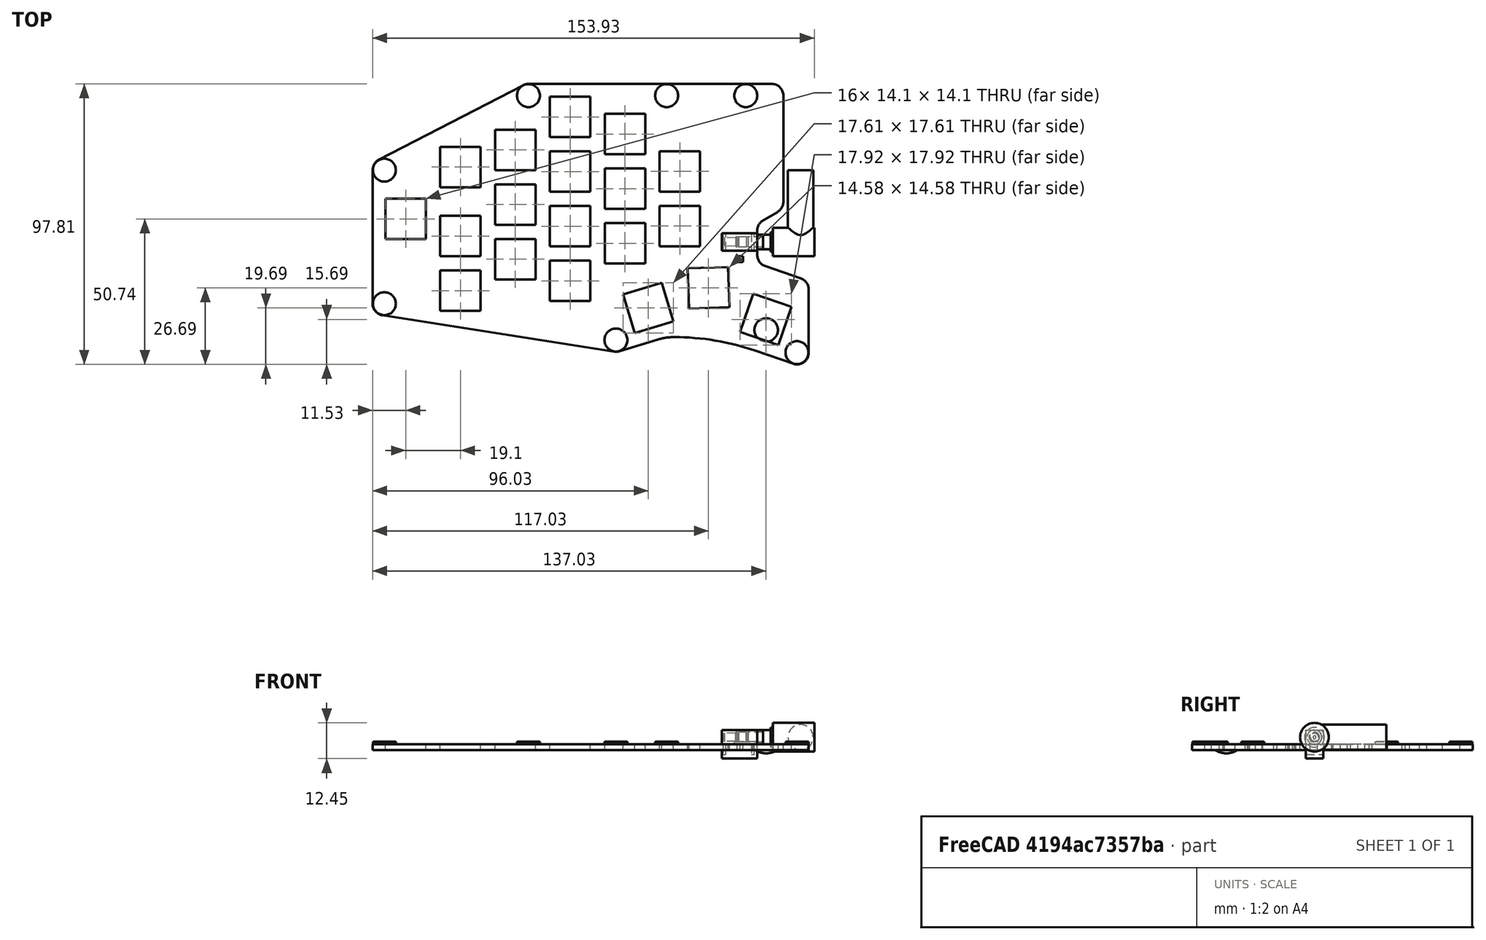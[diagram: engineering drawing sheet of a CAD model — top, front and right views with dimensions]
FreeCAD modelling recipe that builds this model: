
FCSTD DOCUMENT  (FreeCAD 0.21R33771 (Git))
Label: diy-keyboard
License: All rights reserved
LicenseURL: http://en.wikipedia.org/wiki/All_rights_reserved
objects: Sketcher::SketchObject×11, PartDesign::Pad×7, PartDesign::Body×5, PartDesign::ShapeBinder×3, PartDesign::Revolution×2, PartDesign::Pocket×2, Mesh::Feature×1, TechDraw::DrawSVGTemplate×1, PartDesign::SubShapeBinder×1, TechDraw::DrawViewPart×1, TechDraw::DrawPage×1
note: 42 computed .brp shape members not serialized (recipe doc carries the construction recipe); baked Part::Feature solids carry a one-line shape summary decoded from their .brp

FEATURE [Mesh::Feature] switch_mx
  Placement = pos=(43.4215,-43.9157,18) rot=(0,0,1;5.75959rad)
FEATURE [Sketcher::SketchObject] Sketch001  label="master-keys"
  FullyConstrained = false
  MapMode = 5
  Support = -> [XY_Plane]
  sketch-geometry (181):
    g0: GeomPoint X=-10 Y=-11 Z=0
    g1: LineSegment StartX=-16.7997 StartY=-18.2917 StartZ=0 EndX=-17.2917 EndY=-4.20034 EndZ=0
    g2: LineSegment StartX=-17.2917 StartY=-4.20034 StartZ=0 EndX=-3.20034 EndY=-3.70825 EndZ=0
    g3: LineSegment StartX=-3.20034 StartY=-3.70825 StartZ=0 EndX=-2.70825 EndY=-17.7997 EndZ=0
    g4: LineSegment StartX=-2.70825 StartY=-17.7997 StartZ=0 EndX=-16.7997 EndY=-18.2917 EndZ=0
    g5: LineSegment StartX=-19.1868 StartY=-20.8516 StartZ=0 EndX=-19.8516 EndY=-1.81322 EndZ=0
    g6: LineSegment StartX=-19.8516 StartY=-1.81322 StartZ=0 EndX=-0.81322 EndY=-1.14838 EndZ=0
    g7: LineSegment StartX=-0.81322 StartY=-1.14838 StartZ=0 EndX=-0.148385 EndY=-20.1868 EndZ=0
    g8: LineSegment StartX=-0.148385 StartY=-20.1868 StartZ=0 EndX=-19.1868 EndY=-20.8516 EndZ=0
    g9: GeomPoint X=-39.1 Y=4.5 Z=0
    g10: LineSegment StartX=-46.15 StartY=-2.55 StartZ=0 EndX=-46.15 EndY=11.55 EndZ=0
    g11: LineSegment StartX=-46.15 StartY=11.55 StartZ=0 EndX=-32.05 EndY=11.55 EndZ=0
    g12: LineSegment StartX=-32.05 StartY=11.55 StartZ=0 EndX=-32.05 EndY=-2.55 EndZ=0
    g13: LineSegment StartX=-32.05 StartY=-2.55 StartZ=0 EndX=-46.15 EndY=-2.55 EndZ=0
    g14: LineSegment StartX=-48.625 StartY=-5.025 StartZ=0 EndX=-48.625 EndY=14.025 EndZ=0
    g15: LineSegment StartX=-48.625 StartY=14.025 StartZ=0 EndX=-29.575 EndY=14.025 EndZ=0
    g16: LineSegment StartX=-29.575 StartY=14.025 StartZ=0 EndX=-29.575 EndY=-5.025 EndZ=0
    g17: LineSegment StartX=-29.575 StartY=-5.025 StartZ=0 EndX=-48.625 EndY=-5.025 EndZ=0
    g18: GeomPoint X=-58.2 Y=10.5 Z=0
    g19: LineSegment StartX=-65.25 StartY=3.45 StartZ=0 EndX=-65.25 EndY=17.55 EndZ=0
    g20: LineSegment StartX=-65.25 StartY=17.55 StartZ=0 EndX=-51.15 EndY=17.55 EndZ=0
    g21: LineSegment StartX=-51.15 StartY=17.55 StartZ=0 EndX=-51.15 EndY=3.45 EndZ=0
    g22: LineSegment StartX=-51.15 StartY=3.45 StartZ=0 EndX=-65.25 EndY=3.45 EndZ=0
    g23: LineSegment StartX=-67.725 StartY=0.975 StartZ=0 EndX=-67.725 EndY=20.025 EndZ=0
    g24: LineSegment StartX=-67.725 StartY=20.025 StartZ=0 EndX=-48.675 EndY=20.025 EndZ=0
    g25: LineSegment StartX=-48.675 StartY=20.025 StartZ=0 EndX=-48.675 EndY=0.975 EndZ=0
    g26: LineSegment StartX=-48.675 StartY=0.975 StartZ=0 EndX=-67.725 EndY=0.975 EndZ=0
    g27: GeomPoint X=-77.3 Y=-1 Z=0
    g28: LineSegment StartX=-84.35 StartY=-8.05 StartZ=0 EndX=-84.35 EndY=6.05 EndZ=0
    g29: LineSegment StartX=-84.35 StartY=6.05 StartZ=0 EndX=-70.25 EndY=6.05 EndZ=0
    g30: LineSegment StartX=-70.25 StartY=6.05 StartZ=0 EndX=-70.25 EndY=-8.05 EndZ=0
    g31: LineSegment StartX=-70.25 StartY=-8.05 StartZ=0 EndX=-84.35 EndY=-8.05 EndZ=0
    g32: LineSegment StartX=-86.825 StartY=-10.525 StartZ=0 EndX=-86.825 EndY=8.525 EndZ=0
    g33: LineSegment StartX=-86.825 StartY=8.525 StartZ=0 EndX=-67.775 EndY=8.525 EndZ=0
    g34: LineSegment StartX=-67.775 StartY=8.525 StartZ=0 EndX=-67.775 EndY=-10.525 EndZ=0
    g35: LineSegment StartX=-67.775 StartY=-10.525 StartZ=0 EndX=-86.825 EndY=-10.525 EndZ=0
    g36: GeomPoint X=-39.1 Y=23.55 Z=0
    g37: LineSegment StartX=-46.15 StartY=16.5 StartZ=0 EndX=-46.15 EndY=30.6 EndZ=0
    g38: LineSegment StartX=-46.15 StartY=30.6 StartZ=0 EndX=-32.05 EndY=30.6 EndZ=0
    g39: LineSegment StartX=-32.05 StartY=30.6 StartZ=0 EndX=-32.05 EndY=16.5 EndZ=0
    g40: LineSegment StartX=-32.05 StartY=16.5 StartZ=0 EndX=-46.15 EndY=16.5 EndZ=0
    g41: LineSegment StartX=-48.625 StartY=14.025 StartZ=0 EndX=-48.625 EndY=33.075 EndZ=0
    g42: LineSegment StartX=-48.625 StartY=33.075 StartZ=0 EndX=-29.575 EndY=33.075 EndZ=0
    g43: LineSegment StartX=-29.575 StartY=33.075 StartZ=0 EndX=-29.575 EndY=14.025 EndZ=0
    g44: LineSegment StartX=-29.575 StartY=14.025 StartZ=0 EndX=-48.625 EndY=14.025 EndZ=0
    g45: GeomPoint X=-20 Y=10.55 Z=0
    g46: LineSegment StartX=-27.05 StartY=3.5 StartZ=0 EndX=-27.05 EndY=17.6 EndZ=0
    g47: LineSegment StartX=-27.05 StartY=17.6 StartZ=0 EndX=-12.95 EndY=17.6 EndZ=0
    g48: LineSegment StartX=-12.95 StartY=17.6 StartZ=0 EndX=-12.95 EndY=3.5 EndZ=0
    g49: LineSegment StartX=-12.95 StartY=3.5 StartZ=0 EndX=-27.05 EndY=3.5 EndZ=0
    g50: LineSegment StartX=-29.525 StartY=1.025 StartZ=0 EndX=-29.525 EndY=20.075 EndZ=0
    g51: LineSegment StartX=-29.525 StartY=20.075 StartZ=0 EndX=-10.475 EndY=20.075 EndZ=0
    g52: LineSegment StartX=-10.475 StartY=20.075 StartZ=0 EndX=-10.475 EndY=1.025 EndZ=0
    g53: LineSegment StartX=-10.475 StartY=1.025 StartZ=0 EndX=-29.525 EndY=1.025 EndZ=0
    g54: GeomPoint X=-20 Y=29.6 Z=0
    g55: LineSegment StartX=-27.05 StartY=22.55 StartZ=0 EndX=-27.05 EndY=36.65 EndZ=0
    g56: LineSegment StartX=-27.05 StartY=36.65 StartZ=0 EndX=-12.95 EndY=36.65 EndZ=0
    g57: LineSegment StartX=-12.95 StartY=36.65 StartZ=0 EndX=-12.95 EndY=22.55 EndZ=0
    g58: LineSegment StartX=-12.95 StartY=22.55 StartZ=0 EndX=-27.05 EndY=22.55 EndZ=0
    g59: LineSegment StartX=-29.525 StartY=20.075 StartZ=0 EndX=-29.525 EndY=39.125 EndZ=0
    g60: LineSegment StartX=-29.525 StartY=39.125 StartZ=0 EndX=-10.475 EndY=39.125 EndZ=0
    g61: LineSegment StartX=-10.475 StartY=39.125 StartZ=0 EndX=-10.475 EndY=20.075 EndZ=0
    g62: LineSegment StartX=-10.475 StartY=20.075 StartZ=0 EndX=-29.525 EndY=20.075 EndZ=0
    g63: GeomPoint X=-39.1 Y=42.6 Z=0
    g64: LineSegment StartX=-46.15 StartY=35.55 StartZ=0 EndX=-46.15 EndY=49.65 EndZ=0
    g65: LineSegment StartX=-46.15 StartY=49.65 StartZ=0 EndX=-32.05 EndY=49.65 EndZ=0
    g66: LineSegment StartX=-32.05 StartY=49.65 StartZ=0 EndX=-32.05 EndY=35.55 EndZ=0
    g67: LineSegment StartX=-32.05 StartY=35.55 StartZ=0 EndX=-46.15 EndY=35.55 EndZ=0
    g68: LineSegment StartX=-48.625 StartY=33.075 StartZ=0 EndX=-48.625 EndY=52.125 EndZ=0
    g69: LineSegment StartX=-48.625 StartY=52.125 StartZ=0 EndX=-29.575 EndY=52.125 EndZ=0
    g70: LineSegment StartX=-29.575 StartY=52.125 StartZ=0 EndX=-29.575 EndY=33.075 EndZ=0
    g71: LineSegment StartX=-29.575 StartY=33.075 StartZ=0 EndX=-48.625 EndY=33.075 EndZ=0
    g72: GeomPoint X=-58.2 Y=29.55 Z=0
    g73: LineSegment StartX=-65.25 StartY=22.5 StartZ=0 EndX=-65.25 EndY=36.6 EndZ=0
    g74: LineSegment StartX=-65.25 StartY=36.6 StartZ=0 EndX=-51.15 EndY=36.6 EndZ=0
    g75: LineSegment StartX=-51.15 StartY=36.6 StartZ=0 EndX=-51.15 EndY=22.5 EndZ=0
    g76: LineSegment StartX=-51.15 StartY=22.5 StartZ=0 EndX=-65.25 EndY=22.5 EndZ=0
    g77: LineSegment StartX=-67.725 StartY=20.025 StartZ=0 EndX=-67.725 EndY=39.075 EndZ=0
    g78: LineSegment StartX=-67.725 StartY=39.075 StartZ=0 EndX=-48.675 EndY=39.075 EndZ=0
    g79: LineSegment StartX=-48.675 StartY=39.075 StartZ=0 EndX=-48.675 EndY=20.025 EndZ=0
    g80: LineSegment StartX=-48.675 StartY=20.025 StartZ=0 EndX=-67.725 EndY=20.025 EndZ=0
    g81: GeomPoint X=-77.3 Y=18.05 Z=0
    g82: LineSegment StartX=-84.35 StartY=11 StartZ=0 EndX=-84.35 EndY=25.1 EndZ=0
    g83: LineSegment StartX=-84.35 StartY=25.1 StartZ=0 EndX=-70.25 EndY=25.1 EndZ=0
    g84: LineSegment StartX=-70.25 StartY=25.1 StartZ=0 EndX=-70.25 EndY=11 EndZ=0
    g85: LineSegment StartX=-70.25 StartY=11 StartZ=0 EndX=-84.35 EndY=11 EndZ=0
    g86: LineSegment StartX=-86.825 StartY=8.525 StartZ=0 EndX=-86.825 EndY=27.575 EndZ=0
    g87: LineSegment StartX=-86.825 StartY=27.575 StartZ=0 EndX=-67.775 EndY=27.575 EndZ=0
    g88: LineSegment StartX=-67.775 StartY=27.575 StartZ=0 EndX=-67.775 EndY=8.525 EndZ=0
    g89: LineSegment StartX=-67.775 StartY=8.525 StartZ=0 EndX=-86.825 EndY=8.525 EndZ=0
    g90: GeomPoint X=-58.2 Y=48.6 Z=0
    g91: LineSegment StartX=-65.25 StartY=41.55 StartZ=0 EndX=-65.25 EndY=55.65 EndZ=0
    g92: LineSegment StartX=-65.25 StartY=55.65 StartZ=0 EndX=-51.15 EndY=55.65 EndZ=0
    g93: LineSegment StartX=-51.15 StartY=55.65 StartZ=0 EndX=-51.15 EndY=41.55 EndZ=0
    g94: LineSegment StartX=-51.15 StartY=41.55 StartZ=0 EndX=-65.25 EndY=41.55 EndZ=0
    g95: LineSegment StartX=-67.725 StartY=39.075 StartZ=0 EndX=-67.725 EndY=58.125 EndZ=0
    g96: LineSegment StartX=-67.725 StartY=58.125 StartZ=0 EndX=-48.675 EndY=58.125 EndZ=0
    g97: LineSegment StartX=-48.675 StartY=58.125 StartZ=0 EndX=-48.675 EndY=39.075 EndZ=0
    g98: LineSegment StartX=-48.675 StartY=39.075 StartZ=0 EndX=-67.725 EndY=39.075 EndZ=0
    g99: GeomPoint X=-77.3 Y=37.1 Z=0
    g100: LineSegment StartX=-84.35 StartY=30.05 StartZ=0 EndX=-84.35 EndY=44.15 EndZ=0
    g101: LineSegment StartX=-84.35 StartY=44.15 StartZ=0 EndX=-70.25 EndY=44.15 EndZ=0
    g102: LineSegment StartX=-70.25 StartY=44.15 StartZ=0 EndX=-70.25 EndY=30.05 EndZ=0
    g103: LineSegment StartX=-70.25 StartY=30.05 StartZ=0 EndX=-84.35 EndY=30.05 EndZ=0
    g104: LineSegment StartX=-86.825 StartY=27.575 StartZ=0 EndX=-86.825 EndY=46.625 EndZ=0
    g105: LineSegment StartX=-86.825 StartY=46.625 StartZ=0 EndX=-67.775 EndY=46.625 EndZ=0
    g106: LineSegment StartX=-67.775 StartY=46.625 StartZ=0 EndX=-67.775 EndY=27.575 EndZ=0
    g107: LineSegment StartX=-67.775 StartY=27.575 StartZ=0 EndX=-86.825 EndY=27.575 EndZ=0
    g108: GeomPoint X=-31 Y=-18 Z=0
    g109: LineSegment StartX=-35.6807 StartY=-26.8032 StartZ=0 EndX=-39.8032 EndY=-13.3193 EndZ=0
    g110: LineSegment StartX=-39.8032 StartY=-13.3193 StartZ=0 EndX=-26.3193 EndY=-9.19683 EndZ=0
    g111: LineSegment StartX=-26.3193 StartY=-9.19683 StartZ=0 EndX=-22.1968 EndY=-22.6807 EndZ=0
    g112: LineSegment StartX=-22.1968 StartY=-22.6807 StartZ=0 EndX=-35.6807 EndY=-26.8032 EndZ=0
    g113: LineSegment StartX=-37.324 StartY=-29.8936 StartZ=0 EndX=-42.8936 EndY=-11.676 EndZ=0
    g114: LineSegment StartX=-42.8936 StartY=-11.676 StartZ=0 EndX=-24.676 EndY=-6.10636 EndZ=0
    g115: LineSegment StartX=-24.676 StartY=-6.10636 StartZ=0 EndX=-19.1064 EndY=-24.324 EndZ=0
    g116: LineSegment StartX=-19.1064 StartY=-24.324 StartZ=0 EndX=-37.324 EndY=-29.8936 EndZ=0
    g117: GeomPoint X=10 Y=-22 Z=0
    g118: LineSegment StartX=1.03884 StartY=-26.3707 StartZ=0 EndX=5.62935 EndY=-13.0388 EndZ=0
    g119: LineSegment StartX=5.62935 StartY=-13.0388 StartZ=0 EndX=18.9612 EndY=-17.6293 EndZ=0
    g120: LineSegment StartX=18.9612 StartY=-17.6293 StartZ=0 EndX=14.3707 EndY=-30.9612 EndZ=0
    g121: LineSegment StartX=14.3707 StartY=-30.9612 StartZ=0 EndX=1.03884 EndY=-26.3707 EndZ=0
    g122: LineSegment StartX=-2.1071 StartY=-27.905 StartZ=0 EndX=4.09497 EndY=-9.8929 EndZ=0
    g123: LineSegment StartX=4.09497 StartY=-9.8929 StartZ=0 EndX=22.1071 EndY=-16.095 EndZ=0
    g124: LineSegment StartX=22.1071 StartY=-16.095 StartZ=0 EndX=15.905 EndY=-34.1071 EndZ=0
    g125: LineSegment StartX=15.905 StartY=-34.1071 StartZ=0 EndX=-2.1071 EndY=-27.905 EndZ=0
    g126: LineSegment StartX=-20 StartY=0 StartZ=0 EndX=-20 EndY=120 EndZ=0
    g127: LineSegment StartX=-39.1 StartY=0 StartZ=0 EndX=-39.1 EndY=120 EndZ=0
    g128: LineSegment StartX=-58.2 StartY=0 StartZ=0 EndX=-58.2 EndY=120 EndZ=0
    g129: LineSegment StartX=-77.3 StartY=0 StartZ=0 EndX=-77.3 EndY=120 EndZ=0
    g130: LineSegment StartX=-96.4 StartY=0 StartZ=0 EndX=-96.4 EndY=120 EndZ=0
    g131: GeomPoint X=-96.4 Y=-12 Z=0
    g132: LineSegment StartX=-103.45 StartY=-19.05 StartZ=0 EndX=-103.45 EndY=-4.95 EndZ=0
    g133: LineSegment StartX=-103.45 StartY=-4.95 StartZ=0 EndX=-89.35 EndY=-4.95 EndZ=0
    g134: LineSegment StartX=-89.35 StartY=-4.95 StartZ=0 EndX=-89.35 EndY=-19.05 EndZ=0
    g135: LineSegment StartX=-89.35 StartY=-19.05 StartZ=0 EndX=-103.45 EndY=-19.05 EndZ=0
    g136: LineSegment StartX=-105.925 StartY=-21.525 StartZ=0 EndX=-105.925 EndY=-2.475 EndZ=0
    g137: LineSegment StartX=-105.925 StartY=-2.475 StartZ=0 EndX=-86.875 EndY=-2.475 EndZ=0
    g138: LineSegment StartX=-86.875 StartY=-2.475 StartZ=0 EndX=-86.875 EndY=-21.525 EndZ=0
    g139: LineSegment StartX=-86.875 StartY=-21.525 StartZ=0 EndX=-105.925 EndY=-21.525 EndZ=0
    g140: GeomPoint X=-96.4 Y=7.05 Z=0
    g141: LineSegment StartX=-103.45 StartY=-5.4e-15 StartZ=0 EndX=-103.45 EndY=14.1 EndZ=0
    g142: LineSegment StartX=-103.45 StartY=14.1 StartZ=0 EndX=-89.35 EndY=14.1 EndZ=0
    g143: LineSegment StartX=-89.35 StartY=14.1 StartZ=0 EndX=-89.35 EndY=-1.8e-15 EndZ=0
    g144: LineSegment StartX=-89.35 StartY=-1.8e-15 StartZ=0 EndX=-103.45 EndY=-5.4e-15 EndZ=0
    g145: LineSegment StartX=-105.925 StartY=-2.475 StartZ=0 EndX=-105.925 EndY=16.575 EndZ=0
    g146: LineSegment StartX=-105.925 StartY=16.575 StartZ=0 EndX=-86.875 EndY=16.575 EndZ=0
    g147: LineSegment StartX=-86.875 StartY=16.575 StartZ=0 EndX=-86.875 EndY=-2.475 EndZ=0
    g148: LineSegment StartX=-86.875 StartY=-2.475 StartZ=0 EndX=-105.925 EndY=-2.475 EndZ=0
    g149: GeomPoint X=13.565 Y=0 Z=0
    g150: LineSegment StartX=-10 StartY=-11 StartZ=0 EndX=-10 EndY=9 EndZ=0
    g151: LineSegment StartX=-31 StartY=-18 StartZ=0 EndX=-31 EndY=2 EndZ=0
    g152: LineSegment StartX=10 StartY=-22 StartZ=0 EndX=10 EndY=-2 EndZ=0
    g153: LineSegment StartX=-1.50591 StartY=-29.2306 StartZ=0 EndX=-1.16158 EndY=-28.2306 EndZ=0
    g154: GeomPoint X=-96.4 Y=31.1 Z=0
    g155: LineSegment StartX=-103.45 StartY=24.05 StartZ=0 EndX=-103.45 EndY=38.15 EndZ=0
    g156: LineSegment StartX=-103.45 StartY=38.15 StartZ=0 EndX=-89.35 EndY=38.15 EndZ=0
    g157: LineSegment StartX=-89.35 StartY=38.15 StartZ=0 EndX=-89.35 EndY=24.05 EndZ=0
    g158: LineSegment StartX=-89.35 StartY=24.05 StartZ=0 EndX=-103.45 EndY=24.05 EndZ=0
    g159: LineSegment StartX=-105.925 StartY=21.575 StartZ=0 EndX=-105.925 EndY=40.625 EndZ=0
    g160: LineSegment StartX=-105.925 StartY=40.625 StartZ=0 EndX=-86.875 EndY=40.625 EndZ=0
    g161: LineSegment StartX=-86.875 StartY=40.625 StartZ=0 EndX=-86.875 EndY=21.575 EndZ=0
    g162: LineSegment StartX=-86.875 StartY=21.575 StartZ=0 EndX=-105.925 EndY=21.575 EndZ=0
    g163: GeomPoint X=-115.5 Y=13.05 Z=0
    g164: LineSegment StartX=-122.55 StartY=6 StartZ=0 EndX=-122.55 EndY=20.1 EndZ=0
    g165: LineSegment StartX=-122.55 StartY=20.1 StartZ=0 EndX=-108.45 EndY=20.1 EndZ=0
    g166: LineSegment StartX=-108.45 StartY=20.1 StartZ=0 EndX=-108.45 EndY=6 EndZ=0
    g167: LineSegment StartX=-108.45 StartY=6 StartZ=0 EndX=-122.55 EndY=6 EndZ=0
    g168: LineSegment StartX=-125.025 StartY=1.05 StartZ=0 EndX=-125.025 EndY=25.05 EndZ=0
    g169: LineSegment StartX=-125.025 StartY=25.05 StartZ=0 EndX=-105.975 EndY=25.05 EndZ=0
    g170: LineSegment StartX=-105.975 StartY=25.05 StartZ=0 EndX=-105.975 EndY=1.05 EndZ=0
    g171: LineSegment StartX=-105.975 StartY=1.05 StartZ=0 EndX=-125.025 EndY=1.05 EndZ=0
    g172: GeomPoint X=-58.2 Y=-8.55 Z=0
    g173: LineSegment StartX=-65.25 StartY=-15.6 StartZ=0 EndX=-65.25 EndY=-1.5 EndZ=0
    g174: LineSegment StartX=-65.25 StartY=-1.5 StartZ=0 EndX=-51.15 EndY=-1.5 EndZ=0
    g175: LineSegment StartX=-51.15 StartY=-1.5 StartZ=0 EndX=-51.15 EndY=-15.6 EndZ=0
    g176: LineSegment StartX=-51.15 StartY=-15.6 StartZ=0 EndX=-65.25 EndY=-15.6 EndZ=0
    g177: LineSegment StartX=-67.725 StartY=-18.075 StartZ=0 EndX=-67.725 EndY=0.975 EndZ=0
    g178: LineSegment StartX=-67.725 StartY=0.975 StartZ=0 EndX=-48.675 EndY=0.975 EndZ=0
    g179: LineSegment StartX=-48.675 StartY=0.975 StartZ=0 EndX=-48.675 EndY=-18.075 EndZ=0
    g180: LineSegment StartX=-48.675 StartY=-18.075 StartZ=0 EndX=-67.725 EndY=-18.075 EndZ=0
  constraints (453):
    c: Coincident(g1,g2)
    c: Coincident(g2,g3)
    c: Coincident(g3,g4)
    c: Coincident(g4,g1)
    c: Coincident(g5,g6)
    c: Coincident(g6,g7)
    c: Coincident(g7,g8)
    c: Coincident(g8,g5)
    c: Symmetric(g1,g3,g0)
    c: Symmetric(g5,g7,g0)
    c: Symmetric(g1,g2,g0)
    c: Symmetric(g5,g6,g0)
    c: Distance(g4) = 14.1
    c: Distance(g8) = 19.05
    c: Equal(g4,g1)
    c: Equal(g8,g5)
    c: Perpendicular(g1,g4)
    c: Parallel(g4,g8)
    c: Parallel(g1,g5)
    c: Coincident(g10,g11)
    c: Coincident(g11,g12)
    c: Coincident(g12,g13)
    c: Coincident(g13,g10)
    c: Coincident(g14,g15)
    c: Coincident(g15,g16)
    c: Coincident(g16,g17)
    c: Coincident(g17,g14)
    c: Symmetric(g10,g12,g9)
    c: Symmetric(g14,g16,g9)
    c: Symmetric(g10,g11,g9)
    c: Symmetric(g14,g15,g9)
    c: Equal(g4,g13) = 14
    c: Equal(g8,g17) = 19.05
    c: Equal(g13,g10)
    c: Equal(g17,g14)
    c: Perpendicular(g10,g13)
    c: Parallel(g13,g17)
    c: Parallel(g10,g14)
    c: Coincident(g19,g20)
    c: Coincident(g20,g21)
    c: Coincident(g21,g22)
    c: Coincident(g22,g19)
    c: Coincident(g23,g24)
    c: Coincident(g24,g25)
    c: Coincident(g25,g26)
    c: Coincident(g26,g23)
    c: Symmetric(g19,g21,g18)
    c: Symmetric(g23,g25,g18)
    c: Symmetric(g19,g20,g18)
    c: Symmetric(g23,g24,g18)
    c: Equal(g4,g22) = 14
    c: Equal(g8,g26) = 19.05
    c: Equal(g22,g19)
    c: Equal(g26,g23)
    c: Perpendicular(g19,g22)
    c: Parallel(g22,g26)
    c: Parallel(g19,g23)
    c: Coincident(g28,g29)
    c: Coincident(g29,g30)
    c: Coincident(g30,g31)
    c: Coincident(g31,g28)
    c: Coincident(g32,g33)
    c: Coincident(g33,g34)
    c: Coincident(g34,g35)
    c: Coincident(g35,g32)
    c: Symmetric(g28,g30,g27)
    c: Symmetric(g32,g34,g27)
    c: Symmetric(g28,g29,g27)
    c: Symmetric(g32,g33,g27)
    c: Equal(g4,g31) = 14
    c: Equal(g8,g35) = 19.05
    c: Equal(g31,g28)
    c: Equal(g35,g32)
    c: Perpendicular(g28,g31)
    c: Parallel(g31,g35)
    c: Parallel(g28,g32)
    c: Coincident(g37,g38)
    c: Coincident(g38,g39)
    c: Coincident(g39,g40)
    c: Coincident(g40,g37)
    c: Coincident(g41,g42)
    c: Coincident(g42,g43)
    c: Coincident(g43,g44)
    c: Coincident(g44,g41)
    c: Symmetric(g37,g39,g36)
    c: Symmetric(g41,g43,g36)
    c: Symmetric(g37,g38,g36)
    c: Symmetric(g41,g42,g36)
    c: Equal(g4,g40) = 14
    c: Equal(g8,g44) = 19.05
    c: Equal(g40,g37)
    c: Equal(g44,g41)
    c: Perpendicular(g37,g40)
    c: Parallel(g40,g44)
    c: Parallel(g37,g41)
    c: Coincident(g46,g47)
    c: Coincident(g47,g48)
    c: Coincident(g48,g49)
    c: Coincident(g49,g46)
    c: Coincident(g50,g51)
    c: Coincident(g51,g52)
    c: Coincident(g52,g53)
    c: Coincident(g53,g50)
    c: Symmetric(g46,g48,g45)
    c: Symmetric(g50,g52,g45)
    c: Symmetric(g46,g47,g45)
    c: Symmetric(g50,g51,g45)
    c: Equal(g4,g49) = 14
    c: Equal(g8,g53) = 19.05
    c: Equal(g49,g46)
    c: Equal(g53,g50)
    c: Perpendicular(g46,g49)
    c: Parallel(g49,g53)
    c: Parallel(g46,g50)
    c: Coincident(g55,g56)
    c: Coincident(g56,g57)
    c: Coincident(g57,g58)
    c: Coincident(g58,g55)
    c: Coincident(g59,g60)
    c: Coincident(g60,g61)
    c: Coincident(g61,g62)
    c: Coincident(g62,g59)
    c: Symmetric(g55,g57,g54)
    c: Symmetric(g59,g61,g54)
    c: Symmetric(g55,g56,g54)
    c: Symmetric(g59,g60,g54)
    c: Equal(g4,g58) = 14
    c: Equal(g8,g62) = 19.05
    c: Equal(g58,g55)
    c: Equal(g62,g59)
    c: Perpendicular(g55,g58)
    c: Parallel(g58,g62)
    c: Parallel(g55,g59)
    c: Coincident(g64,g65)
    c: Coincident(g65,g66)
    c: Coincident(g66,g67)
    c: Coincident(g67,g64)
    c: Coincident(g68,g69)
    c: Coincident(g69,g70)
    c: Coincident(g70,g71)
    c: Coincident(g71,g68)
    c: Symmetric(g64,g66,g63)
    c: Symmetric(g68,g70,g63)
    c: Symmetric(g64,g65,g63)
    c: Symmetric(g68,g69,g63)
    c: Equal(g4,g67) = 14
    c: Equal(g8,g71) = 19.05
    c: Equal(g67,g64)
    c: Equal(g71,g68)
    c: Perpendicular(g64,g67)
    c: Parallel(g67,g71)
    c: Parallel(g64,g68)
    c: Coincident(g73,g74)
    c: Coincident(g74,g75)
    c: Coincident(g75,g76)
    c: Coincident(g76,g73)
    c: Coincident(g77,g78)
    c: Coincident(g78,g79)
    c: Coincident(g79,g80)
    c: Coincident(g80,g77)
    c: Symmetric(g73,g75,g72)
    c: Symmetric(g77,g79,g72)
    c: Symmetric(g73,g74,g72)
    c: Symmetric(g77,g78,g72)
    c: Equal(g4,g76) = 14
    c: Equal(g8,g80) = 19.05
    c: Equal(g76,g73)
    c: Equal(g80,g77)
    c: Perpendicular(g73,g76)
    c: Parallel(g76,g80)
    c: Parallel(g73,g77)
    c: Coincident(g82,g83)
    c: Coincident(g83,g84)
    c: Coincident(g84,g85)
    c: Coincident(g85,g82)
    c: Coincident(g86,g87)
    c: Coincident(g87,g88)
    c: Coincident(g88,g89)
    c: Coincident(g89,g86)
    c: Symmetric(g82,g84,g81)
    c: Symmetric(g86,g88,g81)
    c: Symmetric(g82,g83,g81)
    c: Symmetric(g86,g87,g81)
    c: Equal(g4,g85) = 14
    c: Equal(g8,g89) = 19.05
    c: Equal(g85,g82)
    c: Equal(g89,g86)
    c: Perpendicular(g82,g85)
    c: Parallel(g85,g89)
    c: Parallel(g82,g86)
    c: Coincident(g91,g92)
    c: Coincident(g92,g93)
    c: Coincident(g93,g94)
    c: Coincident(g94,g91)
    c: Coincident(g95,g96)
    c: Coincident(g96,g97)
    c: Coincident(g97,g98)
    c: Coincident(g98,g95)
    c: Symmetric(g91,g93,g90)
    c: Symmetric(g95,g97,g90)
    c: Symmetric(g91,g92,g90)
    c: Symmetric(g95,g96,g90)
    c: Equal(g4,g94) = 14
    c: Equal(g8,g98) = 19.05
    c: Equal(g94,g91)
    c: Equal(g98,g95)
    c: Perpendicular(g91,g94)
    c: Parallel(g94,g98)
    c: Parallel(g91,g95)
    c: Coincident(g100,g101)
    c: Coincident(g101,g102)
    c: Coincident(g102,g103)
    c: Coincident(g103,g100)
    c: Coincident(g104,g105)
    c: Coincident(g105,g106)
    c: Coincident(g106,g107)
    c: Coincident(g107,g104)
    c: Symmetric(g100,g102,g99)
    c: Symmetric(g104,g106,g99)
    c: Symmetric(g100,g101,g99)
    c: Symmetric(g104,g105,g99)
    c: Equal(g4,g103) = 14
    c: Equal(g8,g107) = 19.05
    c: Equal(g103,g100)
    c: Equal(g107,g104)
    c: Perpendicular(g100,g103)
    c: Parallel(g103,g107)
    c: Parallel(g100,g104)
    c: Coincident(g109,g110)
    c: Coincident(g110,g111)
    c: Coincident(g111,g112)
    c: Coincident(g112,g109)
    c: Coincident(g113,g114)
    c: Coincident(g114,g115)
    c: Coincident(g115,g116)
    c: Coincident(g116,g113)
    c: Symmetric(g109,g111,g108)
    c: Symmetric(g113,g115,g108)
    c: Symmetric(g109,g110,g108)
    c: Symmetric(g113,g114,g108)
    c: Equal(g4,g112) = 14
    c: Equal(g8,g116) = 19.05
    c: Equal(g112,g109)
    c: Equal(g116,g113)
    c: Perpendicular(g109,g112)
    c: Parallel(g112,g116)
    c: Parallel(g109,g113)
    c: Coincident(g118,g119)
    c: Coincident(g119,g120)
    c: Coincident(g120,g121)
    c: Coincident(g121,g118)
    c: Coincident(g122,g123)
    c: Coincident(g123,g124)
    c: Coincident(g124,g125)
    c: Coincident(g125,g122)
    c: Symmetric(g118,g120,g117)
    c: Symmetric(g122,g124,g117)
    c: Symmetric(g118,g119,g117)
    c: Symmetric(g122,g123,g117)
    c: Equal(g4,g121) = 14
    c: Equal(g8,g125) = 19.05
    c: Equal(g121,g118)
    c: Equal(g125,g122)
    c: Perpendicular(g118,g121)
    c: Parallel(g121,g125)
    c: Parallel(g118,g122)
    c: PointOnObject(g126,g-1)
    c: DistanceY(g126,g126) = 120
    c: PointOnObject(g45,g126)
    c: PointOnObject(g54,g126)
    c: Distance(g45,g54) = 19.05
    c: PointOnObject(g127,g-1)
    c: Horizontal(g127,g126)
    c: PointOnObject(g128,g-1)
    c: PointOnObject(g129,g-1)
    c: Horizontal(g129,g128)
    c: Horizontal(g128,g127)
    c: PointOnObject(g9,g127)
    c: PointOnObject(g36,g127)
    c: PointOnObject(g63,g127)
    c: PointOnObject(g18,g128)
    c: PointOnObject(g72,g128)
    c: PointOnObject(g90,g128)
    c: PointOnObject(g27,g129)
    c: PointOnObject(g81,g129)
    c: PointOnObject(g99,g129)
    c: Parallel(g70,g127)
    c: Parallel(g43,g127)
    c: Parallel(g127,g16)
    c: Distance(g9,g36) = 19.05
    c: Distance(g36,g63) = 19.05
    c: Parallel(g25,g128)
    c: Parallel(g79,g128)
    c: Parallel(g97,g128)
    c: Parallel(g106,g129)
    c: Parallel(g88,g129)
    c: Parallel(g34,g129)
    c: Distance(g18,g72) = 19.05
    c: Distance(g72,g90) = 19.05
    c: Distance(g27,g81) = 19.05
    c: Distance(g81,g99) = 19.05
    c: Angle(g-1,g128) = 1.5708
    c: Angle(g-1,g129) = 1.5708
    c: PointOnObject(g130,g-1)
    c: Horizontal(g130,g129)
    c: Angle(g-1,g130) = 1.5708
    c: Coincident(g132,g133)
    c: Coincident(g133,g134)
    c: Coincident(g134,g135)
    c: Coincident(g135,g132)
    c: Coincident(g136,g137)
    c: Coincident(g137,g138)
    c: Coincident(g138,g139)
    c: Coincident(g139,g136)
    c: Symmetric(g132,g134,g131)
    c: Symmetric(g136,g138,g131)
    c: Symmetric(g132,g133,g131)
    c: Symmetric(g136,g137,g131)
    c: Equal(g4,g135) = 14
    c: Equal(g8,g139) = 19.05
    c: Equal(g135,g132)
    c: Equal(g139,g136)
    c: Perpendicular(g132,g135)
    c: Parallel(g135,g139)
    c: Parallel(g132,g136)
    c: Coincident(g141,g142)
    c: Coincident(g142,g143)
    c: Coincident(g143,g144)
    c: Coincident(g144,g141)
    c: Coincident(g145,g146)
    c: Coincident(g146,g147)
    c: Coincident(g147,g148)
    c: Coincident(g148,g145)
    c: Symmetric(g141,g143,g140)
    c: Symmetric(g145,g147,g140)
    c: Symmetric(g141,g142,g140)
    c: Symmetric(g145,g146,g140)
    c: Equal(g4,g144) = 14
    c: Equal(g8,g148) = 19.05
    c: Equal(g144,g141)
    c: Equal(g148,g145)
    c: Perpendicular(g141,g144)
    c: Parallel(g144,g148)
    c: Parallel(g141,g145)
    c: PointOnObject(g140,g130)
    c: PointOnObject(g131,g130)
    c: Parallel(g138,g130)
    c: Parallel(g130,g147)
    c: Distance(g140,g131) = 19.05
    c: Perpendicular(g-1,g127)
    c: Parallel(g61,g126)
    c: Parallel(g52,g126)
    c: Parallel(g126,g127)
    c: DistanceX(g127,g126) = 19.1
    c: DistanceY(g127,g9) = 4.5
    c: DistanceX(g128,g127) = 19.1
    c: DistanceY(g128,g18) = 10.5
    c: DistanceX(g129,g128) = 19.1
    c: DistanceY(g129,g27) = -1
    c: DistanceX(g130,g129) = 19.1
    c: PointOnObject(g149,g-1)
    c: DistanceX(g126,g-1) = 20
    c: DistanceX(g0,g-1) = 10
    c: DistanceY(g117,g-1) = 22
    c: DistanceY(g108,g-1) = 18
    c: Coincident(g150,g0)
    c: Vertical(g150)
    c: Coincident(g151,g108)
    c: Coincident(g152,g117)
    c: Vertical(g152)
    c: Vertical(g151)
    c: Equal(g151,g150)
    c: Equal(g150,g152)
    c: DistanceY(g152,g152) = 20
    c: Angle(g151,g111) = 0.296706
    c: DistanceY(g45,g36) = 13
    c: Angle(g120,g152) = 0.331613
    c: PointOnObject(g153,g125)
    c: Perpendicular(g125,g153)
    c: DistanceY(g153,g153) = 1
    c: Distance(g153,g122) = 1
    c: DistanceY(g131,g130) = 12
    c: Coincident(g155,g156)
    c: Coincident(g156,g157)
    c: Coincident(g157,g158)
    c: Coincident(g158,g155)
    c: Coincident(g159,g160)
    c: Coincident(g160,g161)
    c: Coincident(g161,g162)
    c: Coincident(g162,g159)
    c: Symmetric(g155,g157,g154)
    c: Symmetric(g159,g161,g154)
    c: Symmetric(g155,g156,g154)
    c: Symmetric(g159,g160,g154)
    c: Equal(g158,g155)
    c: Equal(g162,g159)
    c: Perpendicular(g155,g158)
    c: Parallel(g158,g162)
    c: Parallel(g155,g159)
    c: PointOnObject(g154,g130)
    c: Parallel(g157,g130)
    c: Equal(g162,g146)
    c: Equal(g158,g142)
    c: Angle(g150,g3) = 0.0349066
    c: DistanceY(g0,g-1) = 11
    c: DistanceX(g0,g117) = 20
    c: DistanceX(g108,g0) = 21
    c: Coincident(g164,g165)
    c: Coincident(g165,g166)
    c: Coincident(g166,g167)
    c: Coincident(g167,g164)
    c: Coincident(g168,g169)
    c: Coincident(g169,g170)
    c: Coincident(g170,g171)
    c: Coincident(g171,g168)
    c: Symmetric(g164,g166,g163)
    c: Symmetric(g168,g170,g163)
    c: Symmetric(g164,g165,g163)
    c: Symmetric(g168,g169,g163)
    c: Perpendicular(g164,g167)
    c: Parallel(g167,g171)
    c: Parallel(g164,g168)
    c: Equal(g169,g137)
    c: Equal(g165,g133)
    c: Horizontal(g169)
    c: DistanceX(g163,g130) = 19.1
    c: DistanceY(g163,g140) = -6
    c: DistanceY(g168,g168) = 24
    c: Equal(g164,g165)
    c: Coincident(g173,g174)
    c: Coincident(g174,g175)
    c: Coincident(g175,g176)
    c: Coincident(g176,g173)
    c: Coincident(g177,g178)
    c: Coincident(g178,g179)
    c: Coincident(g179,g180)
    c: Coincident(g180,g177)
    c: Symmetric(g173,g175,g172)
    c: Symmetric(g177,g179,g172)
    c: Symmetric(g173,g174,g172)
    c: Symmetric(g177,g178,g172)
    c: Equal(g176,g173)
    c: Equal(g180,g177)
    c: Perpendicular(g173,g176)
    c: Parallel(g176,g180)
    c: Parallel(g173,g177)
    c: Equal(g178,g26)
    c: Equal(g174,g22)
    c: Horizontal(g178)
    c: DistanceY(g172,g18) = 19.05
    c: Vertical(g172,g18)
    c: DistanceY(g154,g99) = 6
    c: DistanceY(g145,g159) = 5
FEATURE [Sketcher::SketchObject] Sketch
  FullyConstrained = false
  MapMode = 5
  Placement = pos=(0,0,0) rot=(1,0,0;1.5708rad)
  Support = -> [XZ_Plane001]
  sketch-geometry (7):
    g0: LineSegment StartX=0 StartY=-1.3 StartZ=0 EndX=0 EndY=0 EndZ=0
    g1: LineSegment StartX=0 StartY=0 StartZ=0 EndX=4.1 EndY=0 EndZ=0
    g2: ArcOfEllipse CenterX=0 CenterY=5.61097 CenterZ=0 NormalX=0 NormalY=0 NormalZ=1 MajorRadius=7.02288 MinorRadius=6.91097 AngleXU=3.14159 StartAngle=1.5708 EndAngle=2.19421
    g3: LineSegment StartX=-7.02288 StartY=5.61097 StartZ=0 EndX=7.02288 EndY=5.61097 EndZ=0
    g4: LineSegment StartX=0 StartY=-1.3 StartZ=0 EndX=0 EndY=12.5219 EndZ=0
    g5: GeomPoint X=-1.24876 Y=5.61097 Z=0
    g6: GeomPoint X=1.24876 Y=5.61097 Z=0
  constraints (11):
    c: Horizontal(g1)
    c: Vertical(g0)
    c: InternalAlignment(g3-g6 -> g2) x4
    c: Coincident(g2,g0)
    c: Coincident(g1,g0)
    c: Coincident(g1,g2)
    c: DistanceX(g1,g1) = 4.1
    c: Coincident(g4,g0)
    c: Vertical(g4)
    c: DistanceY(g0,g0) = 1.3
    c: Coincident(g0,g-1)
FEATURE [PartDesign::Revolution] Revolution
  Angle = 360
  Axis = (0,2e-16,1)
  Base = (0,0,0)
  Placement = pos=(0,0,0) rot=(1,0,0;1.5708rad)
  Profile = -> Sketch
  ReferenceAxis = -> Sketch [V_Axis]
  Reversed = true
FEATURE [PartDesign::Body] Body001  label="rubber-foot"
  Group = -> [Sketch,Revolution]
  Origin = -> Origin001
  Placement = pos=(10.1,-25.7,0.2) rot=(0,0,1;0rad)
  Tip = -> Revolution
FEATURE [Sketcher::SketchObject] Sketch004  label="master-mcu"
  ExternalGeometry = -> [Sketch001]
  FullyConstrained = false
  MapMode = 5
  Support = -> [XY_Plane]
  sketch-geometry (7):
    g0: LineSegment StartX=-6.5 StartY=25.125 StartZ=0 EndX=12.5 EndY=25.125 EndZ=0
    g1: LineSegment StartX=12.5 StartY=25.125 StartZ=0 EndX=12.5 EndY=59.125 EndZ=0
    g2: LineSegment StartX=12.5 StartY=59.125 StartZ=0 EndX=-6.5 EndY=59.125 EndZ=0
    g3: LineSegment StartX=-6.5 StartY=59.125 StartZ=0 EndX=-6.5 EndY=25.125 EndZ=0
    g4: GeomPoint X=-2.62 Y=29.125 Z=0
    g5: GeomPoint X=12.62 Y=29.125 Z=0
    g6: GeomPoint X=3 Y=42.125 Z=0
  constraints (12):
    c: Coincident(g0,g1)
    c: Coincident(g1,g2)
    c: Coincident(g2,g3)
    c: Coincident(g3,g0)
    c: Symmetric(g0,g1,g6)
    c: Symmetric(g0,g2,g6)
    c: Distance(g2) = 19
    c: Distance(g3) = 34
    c: Perpendicular(g3,g2)
    c: DistanceX(g-1,g6) = 3
    c: Horizontal(g2)
    c: DistanceY(g2,g-3) = -7
FEATURE [Sketcher::SketchObject] Sketch005
  FullyConstrained = true
  MapMode = 5
  Placement = pos=(0,0,0) rot=(1,0,0;1.5708rad)
  Support = -> [XZ_Plane002]
  sketch-geometry (4):
    g0: LineSegment StartX=-3.05 StartY=2.55 StartZ=0 EndX=3.05 EndY=2.55 EndZ=0
    g1: LineSegment StartX=3.05 StartY=2.55 StartZ=0 EndX=3.05 EndY=-2.55 EndZ=0
    g2: LineSegment StartX=3.05 StartY=-2.55 StartZ=0 EndX=-3.05 EndY=-2.55 EndZ=0
    g3: LineSegment StartX=-3.05 StartY=-2.55 StartZ=0 EndX=-3.05 EndY=2.55 EndZ=0
  constraints (11):
    c: Coincident(g0,g1)
    c: Coincident(g1,g2)
    c: Coincident(g2,g3)
    c: Coincident(g3,g0)
    c: Horizontal(g0)
    c: Horizontal(g2)
    c: Vertical(g1)
    c: Vertical(g3)
    c: Symmetric(g0,g1,g-1)
    c: DistanceX(g0,g0) = 6.1
    c: DistanceY(g1,g1) = 5.1
FEATURE [PartDesign::Pad] Pad005
  Direction = (0,-1,-2e-16)
  Length = 12.3
  Length2 = 10
  Placement = pos=(0,0,0) rot=(1,0,0;1.5708rad)
  Profile = -> Sketch005
  ReferenceAxis = -> Sketch005 [N_Axis]
  Reversed = true
  Type = 0
FEATURE [Sketcher::SketchObject] Sketch006
  FullyConstrained = false
  MapMode = 5
  Placement = pos=(0,0,0) rot=(1,0,0;1.5708rad)
  Support = -> [XZ_Plane002]
  sketch-geometry (2):
    g0: Circle CenterX=0 CenterY=0 CenterZ=0 NormalX=0 NormalY=0 NormalZ=1 AngleXU=0 Radius=2.55
    g1: Circle CenterX=-0.041022 CenterY=0 CenterZ=0 NormalX=0 NormalY=0 NormalZ=1 AngleXU=0 Radius=1.8
  constraints (4):
    c: Coincident(g0,g-1)
    c: Diameter(g0) = 5.1
    c: PointOnObject(g1,g-1)
    c: Diameter(g1) = 3.6
FEATURE [PartDesign::Pad] Pad006
  BaseFeature = -> Pad005
  Direction = (0,-1,-2e-16)
  Length = 2
  Length2 = 10
  Placement = pos=(0,0,0) rot=(1,0,0;1.5708rad)
  Profile = -> Sketch006
  ReferenceAxis = -> Sketch006 [N_Axis]
  Type = 0
FEATURE [Sketcher::SketchObject] Sketch007
  FullyConstrained = true
  MapMode = 5
  Placement = pos=(0,0,0) rot=(0.57735,0.57735,0.57735;2.0944rad)
  Support = -> [YZ_Plane002]
  sketch-geometry (8):
    g0: LineSegment StartX=1 StartY=0 StartZ=0 EndX=2 EndY=0 EndZ=0
    g1: LineSegment StartX=2 StartY=0 StartZ=0 EndX=2 EndY=-6 EndZ=0
    g2: LineSegment StartX=2 StartY=-6 StartZ=0 EndX=1 EndY=-6 EndZ=0
    g3: LineSegment StartX=1 StartY=-6 StartZ=0 EndX=1 EndY=0 EndZ=0
    g4: LineSegment StartX=11 StartY=0 StartZ=0 EndX=12 EndY=0 EndZ=0
    g5: LineSegment StartX=12 StartY=0 StartZ=0 EndX=12 EndY=-6 EndZ=0
    g6: LineSegment StartX=12 StartY=-6 StartZ=0 EndX=11 EndY=-6 EndZ=0
    g7: LineSegment StartX=11 StartY=-6 StartZ=0 EndX=11 EndY=0 EndZ=0
  constraints (24):
    c: Coincident(g0,g1)
    c: Coincident(g1,g2)
    c: Coincident(g2,g3)
    c: Coincident(g3,g0)
    c: Horizontal(g0)
    c: Horizontal(g2)
    c: Vertical(g1)
    c: Vertical(g3)
    c: Coincident(g4,g5)
    c: Coincident(g5,g6)
    c: Coincident(g6,g7)
    c: Coincident(g7,g4)
    c: Horizontal(g4)
    c: Horizontal(g6)
    c: Vertical(g5)
    c: Vertical(g7)
    c: PointOnObject(g4,g-1)
    c: PointOnObject(g0,g-1)
    c: DistanceX(g2,g2) = 1
    c: Equal(g2,g6)
    c: DistanceY(g3,g3) = 6
    c: Horizontal(g2,g6)
    c: DistanceX(g-1,g0) = 1
    c: DistanceX(g-1,g4) = 11
FEATURE [PartDesign::Pad] Pad007
  BaseFeature = -> Pad006
  Direction = (1,-2e-16,3e-16)
  Length = 6
  Length2 = 10
  Midplane = true
  Placement = pos=(0,0,0) rot=(1,0,0;1.5708rad)
  Profile = -> Sketch007
  ReferenceAxis = -> Sketch007 [N_Axis]
  Type = 0
FEATURE [PartDesign::Body] Body002  label="trrs-connector"
  Group = -> [Sketch005,Pad005,Sketch006,Pad006,Sketch007,Pad007]
  Origin = -> Origin002
  Placement = pos=(7,5,4.5) rot=(0,0,1;1.5708rad)
  Tip = -> Pad007
FEATURE [Sketcher::SketchObject] Sketch015  label="master-pcb-shape"
  ExternalGeometry = -> [Sketch001,Sketch004]
  FullyConstrained = true
  MapMode = 5
  Support = -> [XY_Plane]
  sketch-geometry (35):
    g0: Circle CenterX=-72.725 CenterY=56.025 CenterZ=0 NormalX=0 NormalY=0 NormalZ=1 AngleXU=0 Radius=4
    g1: Circle CenterX=-24.575 CenterY=56.025 CenterZ=0 NormalX=0 NormalY=0 NormalZ=1 AngleXU=0 Radius=4
    g2: Circle CenterX=20.8436 CenterY=-33.5866 CenterZ=0 NormalX=0 NormalY=0 NormalZ=1 AngleXU=0 Radius=4
    g3: Circle CenterX=-42.2413 CenterY=-29.2011 CenterZ=0 NormalX=0 NormalY=0 NormalZ=1 AngleXU=0 Radius=4
    g4: Circle CenterX=-122.925 CenterY=30.05 CenterZ=0 NormalX=0 NormalY=0 NormalZ=1 AngleXU=0 Radius=4
    g5: Circle CenterX=-122.925 CenterY=-16.525 CenterZ=0 NormalX=0 NormalY=0 NormalZ=1 AngleXU=0 Radius=4
    g6: ArcOfCircle CenterX=-72.725 CenterY=56.025 CenterZ=0 NormalX=0 NormalY=0 NormalZ=1 AngleXU=0 Radius=4.1 StartAngle=1.5708 EndAngle=2.04829
    g7: ArcOfCircle CenterX=-122.925 CenterY=30.05 CenterZ=0 NormalX=0 NormalY=0 NormalZ=1 AngleXU=0 Radius=4.1 StartAngle=2.04829 EndAngle=3.14159
    g8: LineSegment StartX=-127.025 StartY=30.05 StartZ=0 EndX=-127.025 EndY=-16.525 EndZ=0
    g9: ArcOfCircle CenterX=-122.925 CenterY=-16.525 CenterZ=0 NormalX=0 NormalY=0 NormalZ=1 AngleXU=0 Radius=4.1 StartAngle=3.14159 EndAngle=4.55655
    g10: ArcOfCircle CenterX=20.8436 CenterY=-33.5866 CenterZ=0 NormalX=0 NormalY=0 NormalZ=1 AngleXU=0 Radius=4.1 StartAngle=4.38078 EndAngle=6.28319
    g11: Circle CenterX=3 CenterY=56.025 CenterZ=0 NormalX=0 NormalY=0 NormalZ=1 AngleXU=0 Radius=4
    g12: LineSegment StartX=-124.809 StartY=33.6914 StartZ=0 EndX=-74.6092 EndY=59.6664 EndZ=0
    g13: ArcOfCircle CenterX=12 CenterY=56.025 CenterZ=0 NormalX=0 NormalY=0 NormalZ=1 AngleXU=0 Radius=4.1 StartAngle=0 EndAngle=1.5708
    g14: LineSegment StartX=24.9436 StartY=-33.5866 StartZ=0 EndX=24.9436 EndY=-11.5866 EndZ=0
    g15: ArcOfCircle CenterX=20.8436 CenterY=-11.5866 CenterZ=0 NormalX=0 NormalY=0 NormalZ=1 AngleXU=0 Radius=4.1 StartAngle=0 EndAngle=1.23918
    g16: ArcOfCircle CenterX=-42.2413 CenterY=-29.2011 CenterZ=0 NormalX=0 NormalY=0 NormalZ=1 AngleXU=0 Radius=4.1 StartAngle=4.55655 EndAngle=5.00909
    g17: LineSegment StartX=-72.725 StartY=60.125 StartZ=0 EndX=12 EndY=60.125 EndZ=0
    g18: LineSegment StartX=-28.2152 StartY=-27.1088 StartZ=0 EndX=-27.6304 EndY=-29.0214 EndZ=0
    g19: LineSegment StartX=6.89896 StartY=-31.0061 StartZ=0 EndX=6.24783 EndY=-32.8971 EndZ=0
    g20: LineSegment StartX=6.24783 StartY=-32.8971 StartZ=0 EndX=19.5087 EndY=-37.4632 EndZ=0
    g21: LineSegment StartX=-41.0426 StartY=-33.1219 StartZ=0 EndX=-27.6304 EndY=-29.0214 EndZ=0
    g22: ArcOfCircle CenterX=-21.9687 CenterY=-47.5399 CenterZ=0 NormalX=0 NormalY=0 NormalZ=1 AngleXU=0 Radius=19.3647 StartAngle=1.5708 EndAngle=1.8675
    g23: ArcOfCircle CenterX=-21.9687 CenterY=-114.844 CenterZ=0 NormalX=0 NormalY=0 NormalZ=1 AngleXU=0 Radius=86.6687 StartAngle=1.23918 EndAngle=1.5708
    g24: LineSegment StartX=3 StartY=56.025 StartZ=0 EndX=3 EndY=59.125 EndZ=0
    g25: LineSegment StartX=16.1 StartY=56.025 StartZ=0 EndX=16.1 EndY=19 EndZ=0
    g26: LineSegment StartX=7 StartY=0.440896 StartZ=0 EndX=7 EndY=9 EndZ=0
    g27: ArcOfCircle CenterX=11.1 CenterY=9 CenterZ=0 NormalX=0 NormalY=0 NormalZ=1 AngleXU=0 Radius=4.1 StartAngle=2.09617 EndAngle=3.14159
    g28: ArcOfCircle CenterX=12 CenterY=19 CenterZ=0 NormalX=0 NormalY=0 NormalZ=1 AngleXU=0 Radius=4.1 StartAngle=5.23776 EndAngle=6.28319
    g29: ArcOfCircle CenterX=11.1 CenterY=0.440896 CenterZ=0 NormalX=0 NormalY=0 NormalZ=1 AngleXU=0 Radius=4.1 StartAngle=3.14159 EndAngle=4.38078
    g30: LineSegment StartX=9.04371 StartY=12.5471 StartZ=0 EndX=14.0563 EndY=15.4529 EndZ=0
    g31: LineSegment StartX=9.76517 StartY=-3.43573 StartZ=0 EndX=22.1784 EndY=-7.70994 EndZ=0
    g32: LineSegment StartX=16.5887 StartY=-32.1215 StartZ=0 EndX=20.8436 EndY=-33.5866 EndZ=0
    g33: LineSegment StartX=-42.2413 StartY=-29.2011 StartZ=0 EndX=-37.9379 EndY=-27.8854 EndZ=0
    g34: LineSegment StartX=-42.8777 StartY=-33.2514 StartZ=0 EndX=-123.561 EndY=-20.5753 EndZ=0
  constraints (95):
    c: Equal(g3,g4)
    c: Equal(g4,g0)
    c: Equal(g0,g1)
    c: Equal(g3,g5)
    c: Tangent(g8,g9) = -1.5708
    c: Coincident(g9,g5)
    c: Coincident(g7,g4)
    c: Equal(g7,g9)
    c: Tangent(g7,g8) = -1.5708
    c: Horizontal(g2,g10)
    c: Coincident(g10,g2)
    c: Equal(g11,g1)
    c: Horizontal(g11,g1)
    c: Diameter(g11) = 8
    c: Radius(g10) = 4.1
    c: Equal(g6,g7)
    c: Horizontal(g13,g13)
    c: Vertical(g13,g13)
    c: Radius(g13) = 4.1
    c: Equal(g9,g10)
    c: Vertical(g8)
    c: Tangent(g12,g7) = 1.5708
    c: Equal(g2,g11)
    c: Coincident(g6,g0)
    c: Tangent(g6,g12) = 1.5708
    c: DistanceX(g-1,g13) = 12
    c: Coincident(g14,g10)
    c: Vertical(g14)
    c: Horizontal(g15,g15)
    c: Coincident(g14,g15)
    c: Coincident(g16,g3)
    c: Coincident(g17,g6)
    c: Horizontal(g17)
    c: Vertical(g6,g0)
    c: Equal(g19,g18)
    c: Distance(g18) = 2
    c: Coincident(g20,g19)
    c: Tangent(g20,g10) = -1.5708
    c: Tangent(g21,g16) = -1.5708
    c: Coincident(g21,g18)
    c: Equal(g16,g10)
    c: Tangent(g22,g21) = 1.5708
    c: Tangent(g23,g20) = 1.5708
    c: Vertical(g23,g22)
    c: Vertical(g22,g22)
    c: Coincident(g22,g23)
    c: Perpendicular(g-3,g19)
    c: Perpendicular(g-9,g18)
    c: Symmetric(g-3,g-6,g19)
    c: Parallel(g20,g-3)
    c: Symmetric(g-9,g-9,g18)
    c: Parallel(g21,g-9)
    c: DistanceX(g8,g-5) = 2
    c: DistanceY(g-5,g4) = 5
    c: DistanceY(g-4,g6) = 2
    c: DistanceX(g0,g-4) = 5
    c: DistanceX(g-8,g1) = 5
    c: Coincident(g24,g11)
    c: Symmetric(g-11,g-11,g24)
    c: Vertical(g24)
    c: Coincident(g25,g13)
    c: Vertical(g25)
    c: Vertical(g26)
    c: Coincident(g27,g26)
    c: Coincident(g28,g25)
    c: Coincident(g29,g26)
    c: Equal(g15,g29)
    c: Equal(g29,g27)
    c: Equal(g27,g28)
    c: Horizontal(g27,g26)
    c: Horizontal(g25,g28)
    c: Equal(g28,g13)
    c: Horizontal(g26,g29)
    c: Tangent(g31,g29) = -1.5708
    c: Tangent(g31,g15) = 1.5708
    c: DistanceX(g-1,g26) = 7
    c: Parallel(g31,g-3)
    c: DistanceY(g14,g14) = 22
    c: Tangent(g30,g28) = -1.5708
    c: Tangent(g30,g27) = 1.5708
    c: DistanceY(g-1,g27) = 9
    c: DistanceY(g-1,g28) = 19
    c: Coincident(g13,g17)
    c: Horizontal(g0,g1)
    c: PointOnObject(g32,g-6)
    c: Coincident(g32,g2)
    c: Perpendicular(g-6,g32)
    c: Distance(g32) = 4.5
    c: Coincident(g33,g3)
    c: PointOnObject(g33,g-7)
    c: Perpendicular(g-7,g33)
    c: Equal(g33,g32)
    c: Tangent(g34,g9) = 1.5708
    c: Tangent(g34,g16) = 1.5708
    c: DistanceY(g-10,g5) = 5
FEATURE [Sketcher::SketchObject] Sketch016
  FullyConstrained = true
  MapMode = 5
  Support = -> [XY_Plane003]
  sketch-geometry (4):
    g0: LineSegment StartX=0 StartY=0 StartZ=0 EndX=2 EndY=0 EndZ=0
    g1: LineSegment StartX=2 StartY=0 StartZ=0 EndX=2 EndY=-2 EndZ=0
    g2: LineSegment StartX=2 StartY=-2 StartZ=0 EndX=0 EndY=-2 EndZ=0
    g3: LineSegment StartX=0 StartY=-2 StartZ=0 EndX=0 EndY=0 EndZ=0
  constraints (11):
    c: Coincident(g0,g1)
    c: Coincident(g1,g2)
    c: Coincident(g2,g3)
    c: Coincident(g3,g0)
    c: Horizontal(g0)
    c: Horizontal(g2)
    c: Vertical(g1)
    c: Vertical(g3)
    c: Coincident(g0,g-1)
    c: DistanceX(g0,g0) = 2
    c: Equal(g1,g0)
FEATURE [TechDraw::DrawSVGTemplate] Template
  EditableTexts = APPROVER_NAME=APPROVER NAME; AUTHOR_NAME=Andrew Fowler; DN=DN; DOCUMENT_TYPE=Mechanical assembly drawing; OWNER_NAME=OWNER NAME; PM=PM; PN=PN; REVISION=REV A; RIGHTS=(R) DO NOT DUPLICATE THIS DRAWING TO THIRD PARTIES WITHOUT OWNER'S PERMISSION !; SCALE=M x:x; SHEET=99 of 99; SIZE=A4; TITLELINE-1=FreeCAD; TOLERANCE=+/- ?
  Height = 210
  Orientation = 1
  Width = 297
FEATURE [Sketcher::SketchObject] Sketch017
  FullyConstrained = true
  MapMode = 5
  Support = -> [XY_Plane004]
  sketch-geometry (21):
    g0: LineSegment StartX=4.8 StartY=0 StartZ=0 EndX=4.8 EndY=5 EndZ=0
    g1: LineSegment StartX=4.8 StartY=5 StartZ=0 EndX=-9.7 EndY=5 EndZ=0
    g2: LineSegment StartX=-9.7 StartY=5 StartZ=0 EndX=-9.7 EndY=3.44 EndZ=0
    g3: LineSegment StartX=-9.7 StartY=3.44 StartZ=0 EndX=-10.4 EndY=3.44 EndZ=0
    g4: LineSegment StartX=-10.4 StartY=3.44 StartZ=0 EndX=-10.4 EndY=2.54 EndZ=0
    g5: LineSegment StartX=-10.4 StartY=2.54 StartZ=0 EndX=-13.05 EndY=2.54 EndZ=0
    g6: LineSegment StartX=-13.05 StartY=2.54 StartZ=0 EndX=-13.05 EndY=1.75 EndZ=0
    g7: LineSegment StartX=-13.05 StartY=1.75 StartZ=0 EndX=-18.35 EndY=1.75 EndZ=0
    g8: LineSegment StartX=-18.35 StartY=1.75 StartZ=0 EndX=-18.35 EndY=1.65 EndZ=0
    g9: LineSegment StartX=-18.35 StartY=1.65 StartZ=0 EndX=-18.95 EndY=1.65 EndZ=0
    g10: LineSegment StartX=-18.95 StartY=1.65 StartZ=0 EndX=-18.95 EndY=1.75 EndZ=0
    g11: LineSegment StartX=-18.95 StartY=1.75 StartZ=0 EndX=-21.55 EndY=1.75 EndZ=0
    g12: LineSegment StartX=-21.55 StartY=1.75 StartZ=0 EndX=-21.55 EndY=1.65 EndZ=0
    g13: LineSegment StartX=-21.55 StartY=1.65 StartZ=0 EndX=-22.15 EndY=1.65 EndZ=0
    g14: LineSegment StartX=-22.15 StartY=1.65 StartZ=0 EndX=-22.15 EndY=1.75 EndZ=0
    g15: LineSegment StartX=-22.15 StartY=1.75 StartZ=0 EndX=-22.65 EndY=1.75 EndZ=0
    g16: LineSegment StartX=-22.65 StartY=1.75 StartZ=0 EndX=-22.65 EndY=1.4 EndZ=0
    g17: LineSegment StartX=-22.65 StartY=1.4 StartZ=0 EndX=-26.55 EndY=1.5 EndZ=0
    g18: LineSegment StartX=-26.55 StartY=1.5 StartZ=0 EndX=-27.05 EndY=0.5 EndZ=0
    g19: LineSegment StartX=-27.05 StartY=0.5 StartZ=0 EndX=-27.05 EndY=0 EndZ=0
    g20: LineSegment StartX=-27.05 StartY=0 StartZ=0 EndX=4.8 EndY=0 EndZ=0
  constraints (64):
    c: PointOnObject(g0,g-1)
    c: Vertical(g0)
    c: Coincident(g0,g1)
    c: Horizontal(g1)
    c: Coincident(g1,g2)
    c: Vertical(g2)
    c: Coincident(g2,g3)
    c: Coincident(g3,g4)
    c: Coincident(g4,g5)
    c: Horizontal(g5)
    c: Coincident(g5,g6)
    c: Vertical(g6)
    c: Coincident(g6,g7)
    c: Horizontal(g7)
    c: Coincident(g7,g8)
    c: Coincident(g8,g9)
    c: Horizontal(g9)
    c: Coincident(g9,g10)
    c: Vertical(g10)
    c: Coincident(g10,g11)
    c: Coincident(g11,g12)
    c: Vertical(g12)
    c: Coincident(g12,g13)
    c: Coincident(g13,g14)
    c: Coincident(g14,g15)
    c: Coincident(g15,g16)
    c: Coincident(g16,g17)
    c: Coincident(g17,g18)
    c: Coincident(g18,g19)
    c: PointOnObject(g19,g-1)
    c: Coincident(g19,g20)
    c: Coincident(g20,g0)
    c: DistanceX(g1,g1) = 14.5
    c: DistanceY(g0,g0) = 5
    c: DistanceX(g-1,g0) = 4.8
    c: Horizontal(g3)
    c: DistanceY(g0,g2) = 3.44
    c: Vertical(g4)
    c: DistanceY(g0,g4) = 2.54
    c: DistanceX(g3,g3) = 0.7
    c: DistanceY(g0,g6) = 1.75
    c: DistanceX(g5,g5) = 2.65
    c: Vertical(g8)
    c: Horizontal(g11)
    c: Vertical(g14)
    c: Vertical(g16)
    c: Horizontal(g10,g7)
    c: Horizontal(g15)
    c: Horizontal(g14,g11)
    c: DistanceX(g7,g7) = 5.3
    c: DistanceX(g9,g9) = 0.6
    c: DistanceX(g15,g5) = 9.6
    c: DistanceX(g15,g15) = 0.5
    c: Equal(g13,g9)
    c: DistanceX(g11,g11) = 2.6
    c: DistanceY(g8,g8) = 0.1
    c: Horizontal(g9,g12)
    c: Horizontal(g13)
    c: Vertical(g19)
    c: DistanceY(g0,g17) = 1.5
    c: DistanceY(g19,g18) = 0.5
    c: DistanceX(g17,g16) = 3.9
    c: DistanceX(g19,g6) = 14
    c: DistanceY(g0,g16) = 1.4
FEATURE [PartDesign::Revolution] Revolution001
  Angle = 360
  Axis = (1,0,0)
  Base = (0,0,0)
  Profile = -> Sketch017
  ReferenceAxis = -> Sketch017 [H_Axis]
FEATURE [Sketcher::SketchObject] Sketch018
  FullyConstrained = true
  MapMode = 5
  Placement = pos=(0,0,0) rot=(1,0,0;1.5708rad)
  Support = -> [XZ_Plane004]
  sketch-geometry (1):
    g0: Circle CenterX=0 CenterY=0 CenterZ=0 NormalX=0 NormalY=0 NormalZ=1 AngleXU=0 Radius=4.4
  constraints (2):
    c: Coincident(g0,g-1)
    c: Diameter(g0) = 8.8
FEATURE [PartDesign::Pad] Pad
  BaseFeature = -> Revolution001
  Direction = (0,-1,2e-16)
  Length = 25
  Length2 = 10
  Profile = -> Sketch018
  ReferenceAxis = -> Sketch018 [N_Axis]
  Reversed = true
  Type = 0
FEATURE [PartDesign::Body] Body004  label="trs-90-connector"
  Group = -> [Sketch017,Revolution001,Sketch018,Pad]
  Origin = -> Origin004
  Placement = pos=(22.1,5,4.5) rot=(0,0,1;0rad)
  Tip = -> Pad
FEATURE [PartDesign::SubShapeBinder] Binder
  BindCopyOnChange = 0
  BindMode = 0
  ClaimChildren = false
  Context = -> Body003 [Binder.]
  Fuse = false
  MakeFace = true
  OffsetFill = false
  OffsetIntersection = false
  OffsetJoinType = 0
  OffsetOpenResult = false
  PartialLoad = false
  Relative = true
  Support = -> [Body002[Pad007.Face1]]
  _Version = 2
FEATURE [Sketcher::SketchObject] Sketch019  label="master-connector"
  FullyConstrained = true
  MapMode = 5
  Support = -> [XY_Plane]
  sketch-geometry (9):
    g0: LineSegment StartX=-5.2 StartY=8 StartZ=0 EndX=7 EndY=8 EndZ=0
    g1: LineSegment StartX=7 StartY=8 StartZ=0 EndX=7 EndY=2 EndZ=0
    g2: LineSegment StartX=7 StartY=2 StartZ=0 EndX=-5.2 EndY=2 EndZ=0
    g3: LineSegment StartX=-5.2 StartY=2 StartZ=0 EndX=-5.2 EndY=8 EndZ=0
    g4: LineSegment StartX=7 StartY=7.5 StartZ=0 EndX=9 EndY=7.5 EndZ=0
    g5: LineSegment StartX=9 StartY=7.5 StartZ=0 EndX=9 EndY=2.5 EndZ=0
    g6: LineSegment StartX=9 StartY=2.5 StartZ=0 EndX=7 EndY=2.5 EndZ=0
    g7: LineSegment StartX=7 StartY=2.5 StartZ=0 EndX=7 EndY=7.5 EndZ=0
    g8: GeomPoint X=7 Y=5 Z=0
  constraints (24):
    c: Coincident(g0,g1)
    c: Coincident(g1,g2)
    c: Coincident(g2,g3)
    c: Coincident(g3,g0)
    c: Horizontal(g0)
    c: Horizontal(g2)
    c: Vertical(g1)
    c: Vertical(g3)
    c: Coincident(g4,g5)
    c: Coincident(g5,g6)
    c: Coincident(g6,g7)
    c: Coincident(g7,g4)
    c: Horizontal(g4)
    c: Horizontal(g6)
    c: Vertical(g5)
    c: Vertical(g7)
    c: DistanceX(g0,g0) = 12.2
    c: DistanceX(g4,g4) = 2
    c: DistanceY(g3,g3) = 6
    c: DistanceY(g5,g5) = 5
    c: Symmetric(g6,g4,g8)
    c: Symmetric(g1,g0,g8)
    c: DistanceX(g-1,g8) = 7
    c: DistanceY(g-1,g8) = 5
FEATURE [PartDesign::Body] Body  label="master"
  Group = -> [Sketch001,Sketch004,Sketch019,Sketch015]
  Origin = -> Origin
FEATURE [PartDesign::ShapeBinder] ShapeBinder018  label="keys-binder"
  Support = -> [Sketch001]
  TraceSupport = false
FEATURE [PartDesign::ShapeBinder] ShapeBinder  label="outline-binder"
  Support = -> [Sketch015]
  TraceSupport = false
FEATURE [PartDesign::Pad] Pad009  label="outline"
  Direction = (0,0,1)
  Length = 2
  Length2 = 10
  Profile = -> ShapeBinder
  Type = 0
FEATURE [PartDesign::ShapeBinder] ShapeBinder019  label="feet-binder"
  Support = -> [Sketch015]
  TraceSupport = false
FEATURE [PartDesign::Pad] Pad010  label="feet"
  BaseFeature = -> Pad009
  Direction = (0,0,1)
  Length = 3
  Length2 = 10
  Profile = -> ShapeBinder019
  Type = 0
FEATURE [PartDesign::Pocket] Pocket  label="keys"
  BaseFeature = -> Pad010
  Direction = (0,0,-1)
  Length = 5
  Length2 = 5
  Profile = -> ShapeBinder018
  Reversed = true
  Type = 1
FEATURE [PartDesign::Pocket] Pocket001  label="zero"
  BaseFeature = -> Pocket
  Direction = (0,0,-1)
  Length = 5
  Length2 = 5
  Profile = -> Sketch016
  ReferenceAxis = -> Sketch016 [N_Axis]
  Reversed = true
  Type = 1
FEATURE [PartDesign::Pad] Pad011  label="trrs"
  BaseFeature = -> Pocket001
  Direction = (-2e-16,0,1)
  Length = 10
  Length2 = 10
  Profile = -> Binder
  Reversed = true
  Type = 0
FEATURE [PartDesign::Body] Body003  label="pcb"
  Group = -> [ShapeBinder,Pad009,ShapeBinder019,Pad010,ShapeBinder018,Pocket,Sketch016,Pocket001,Binder,Pad011]
  Origin = -> Origin003
  Tip = -> Pad011
FEATURE [TechDraw::DrawViewPart] View
  CoarseView = false
  Direction = (0,0,1)
  Focus = 100
  HardHidden = false
  IsoCount = 0
  IsoHidden = false
  IsoVisible = false
  LockPosition = false
  Perspective = false
  Rotation = 0
  ScaleType = 0
  ScrubCount = 0
  SeamHidden = false
  SeamVisible = true
  SmoothHidden = false
  SmoothVisible = true
  Source = -> [Body003]
  X = 103.108
  XDirection = (1,0,0)
  Y = 121.543
FEATURE [TechDraw::DrawPage] Page  label="pcb-outline001"
  KeepUpdated = true
  NextBalloonIndex = 1
  ProjectionType = 0
  Template = -> Template
  Views = -> [View]
